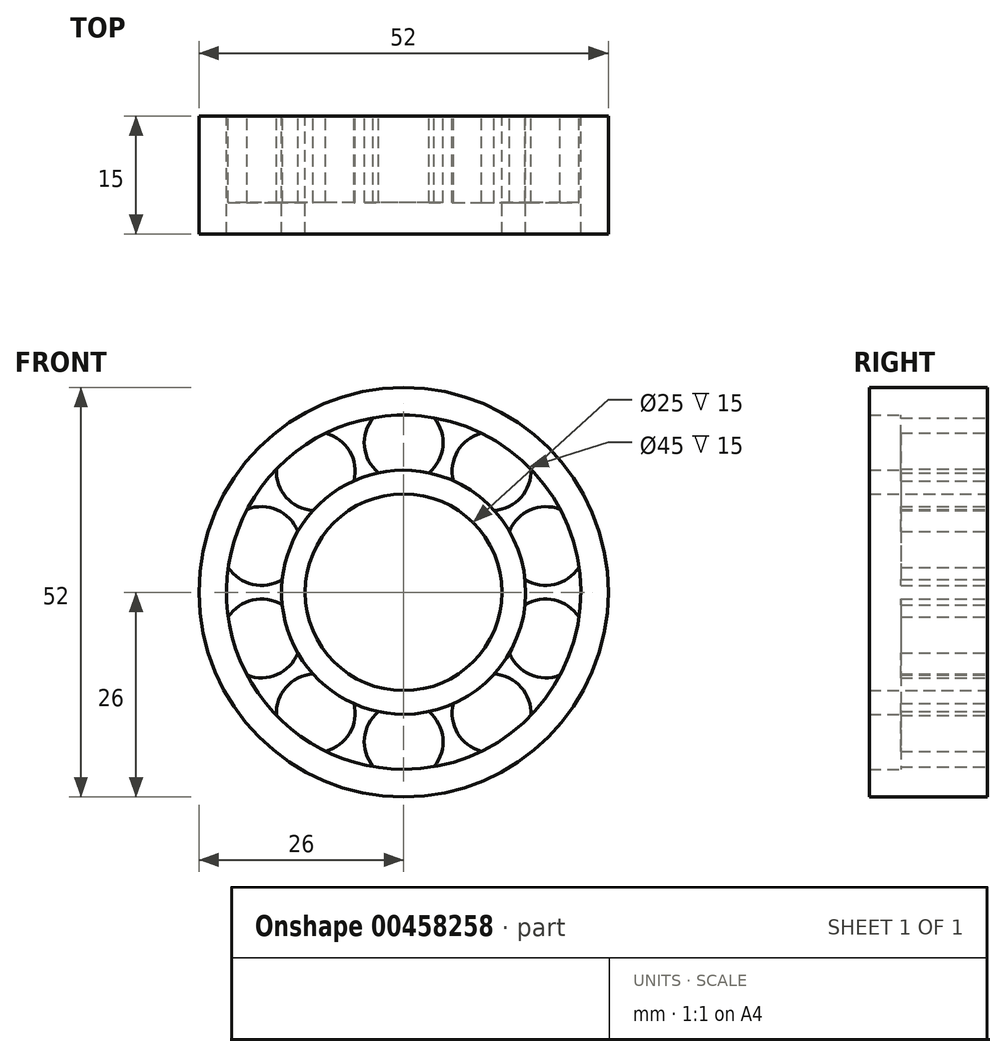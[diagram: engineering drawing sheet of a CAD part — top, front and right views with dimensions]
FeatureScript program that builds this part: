
annotation { "Feature Type Name" : "Feature", "Feature Type Description" : "" }
export const myFeature = defineFeature(function(context is Context, id is Id, definition is map)
    precondition{}
    {
        {
            var Q0;
            Q0=qCreatedBy(makeId("Front.planeOp"),FACE);
            var sketch = newSketch(context, id + "F0", { "sketchPlane" : qUnion([Q0])});
            skCircle(sketch, "E0", {"center": v(0, 0) * mm, "radius": 15.5 * mm});
            skCircle(sketch, "E1", {"center": v(0, 0) * mm, "radius": 12.5 * mm});
            skCircle(sketch, "E2", {"center": v(0, 0) * mm, "radius": 26 * mm});
            skCircle(sketch, "E3", {"center": v(0, 0) * mm, "radius": 22.5 * mm});
            skSolve(sketch);
        }
        {
            var Q0;
            Q0=makeQuery(id+"F0.imprint","IMPRINT",FACE,{"disambiguationData":[TD([[makeQuery(id+"F0.imprint","IMPRINT",EDGE,{"derivedFrom":sQuery(id+"F0.wireOp",EDGE,"E0")}),1.0]])]});
            var Q1;
            Q1=makeQuery(id+"F0.imprint","IMPRINT",FACE,{"disambiguationData":[TD([[makeQuery(id+"F0.imprint","IMPRINT",EDGE,{"derivedFrom":sQuery(id+"F0.wireOp",EDGE,"E2")}),1.0]])]});
            extrude(context, id + "F1", {"entities" : qUnion([Q0, Q1]), "depth" : 15 * mm, "offsetDistance" : 25 * mm});
        }
        {
            var Q0;
            Q0=qCreatedBy(makeId("Front.planeOp"),FACE);
            cPlane(context, id + "F2", {"entities" : qUnion([Q0]), "cplaneType" : CPlaneType.OFFSET, "offset" : 0 * mm, "width" : 150 * mm, "height" : 150 * mm});
        }
        {
            var Q0;
            Q0=qCreatedBy(id+"F2.planeOp",FACE);
            var sketch = newSketch(context, id + "F3", { "sketchPlane" : qUnion([Q0])});
            skCircle(sketch, "E4", {"center": v(0, 19) * mm, "radius": 5 * mm});
            skCircle(sketch, "E5.1.0", {"center": v(-11.17, 15.37) * mm, "radius": 5 * mm});
            skCircle(sketch, "E5.2.0", {"center": v(-18.07, 5.87) * mm, "radius": 5 * mm});
            skCircle(sketch, "E5.3.0", {"center": v(-18.07, -5.87) * mm, "radius": 5 * mm});
            skCircle(sketch, "E5.4.0", {"center": v(-11.17, -15.37) * mm, "radius": 5 * mm});
            skCircle(sketch, "E5.5.0", {"center": v(0, -19) * mm, "radius": 5 * mm});
            skCircle(sketch, "E5.6.0", {"center": v(11.17, -15.37) * mm, "radius": 5 * mm});
            skCircle(sketch, "E5.7.0", {"center": v(18.07, -5.87) * mm, "radius": 5 * mm});
            skCircle(sketch, "E5.8.0", {"center": v(18.07, 5.87) * mm, "radius": 5 * mm});
            skCircle(sketch, "E5.9.0", {"center": v(11.17, 15.37) * mm, "radius": 5 * mm});
            skPoint(sketch, "E5.center", {"position": v(0, 0) * mm});
            skSolve(sketch);
        }
        {
            var Q0;
            Q0=makeQuery(id+"F3.imprint","IMPRINT",FACE,{"disambiguationData":[TD([[makeQuery(id+"F3.imprint","IMPRINT",EDGE,{"derivedFrom":sQuery(id+"F3.wireOp",EDGE,"E4")}),1.0]])]});
            var Q1;
            Q1=makeQuery(id+"F3.imprint","IMPRINT",FACE,{"disambiguationData":[TD([[makeQuery(id+"F3.imprint","IMPRINT",EDGE,{"derivedFrom":sQuery(id+"F3.wireOp",EDGE,"E5.9.0")}),1.0]])]});
            var Q2;
            Q2=makeQuery(id+"F3.imprint","IMPRINT",FACE,{"disambiguationData":[TD([[makeQuery(id+"F3.imprint","IMPRINT",EDGE,{"derivedFrom":sQuery(id+"F3.wireOp",EDGE,"E5.8.0")}),1.0]])]});
            var Q3;
            Q3=makeQuery(id+"F3.imprint","IMPRINT",FACE,{"disambiguationData":[TD([[makeQuery(id+"F3.imprint","IMPRINT",EDGE,{"derivedFrom":sQuery(id+"F3.wireOp",EDGE,"E5.7.0")}),1.0]])]});
            var Q4;
            Q4=makeQuery(id+"F3.imprint","IMPRINT",FACE,{"disambiguationData":[TD([[makeQuery(id+"F3.imprint","IMPRINT",EDGE,{"derivedFrom":sQuery(id+"F3.wireOp",EDGE,"E5.6.0")}),1.0]])]});
            var Q5;
            Q5=makeQuery(id+"F3.imprint","IMPRINT",FACE,{"disambiguationData":[TD([[makeQuery(id+"F3.imprint","IMPRINT",EDGE,{"derivedFrom":sQuery(id+"F3.wireOp",EDGE,"E5.5.0")}),1.0]])]});
            var Q6;
            Q6=makeQuery(id+"F3.imprint","IMPRINT",FACE,{"disambiguationData":[TD([[makeQuery(id+"F3.imprint","IMPRINT",EDGE,{"derivedFrom":sQuery(id+"F3.wireOp",EDGE,"E5.4.0")}),1.0]])]});
            var Q7;
            Q7=makeQuery(id+"F3.imprint","IMPRINT",FACE,{"disambiguationData":[TD([[makeQuery(id+"F3.imprint","IMPRINT",EDGE,{"derivedFrom":sQuery(id+"F3.wireOp",EDGE,"E5.3.0")}),1.0]])]});
            var Q8;
            Q8=makeQuery(id+"F3.imprint","IMPRINT",FACE,{"disambiguationData":[TD([[makeQuery(id+"F3.imprint","IMPRINT",EDGE,{"derivedFrom":sQuery(id+"F3.wireOp",EDGE,"E5.2.0")}),1.0]])]});
            var Q9;
            Q9=makeQuery(id+"F3.imprint","IMPRINT",FACE,{"disambiguationData":[TD([[makeQuery(id+"F3.imprint","IMPRINT",EDGE,{"derivedFrom":sQuery(id+"F3.wireOp",EDGE,"E5.1.0")}),1.0]])]});
            extrude(context, id + "F4", {"entities" : qUnion([Q0, Q1, Q2, Q3, Q4, Q5, Q6, Q7, Q8, Q9]), "operationType" : NewBodyOperationType.ADD, "depth" : 11 * mm, "offsetDistance" : 25 * mm});
        }
    });
